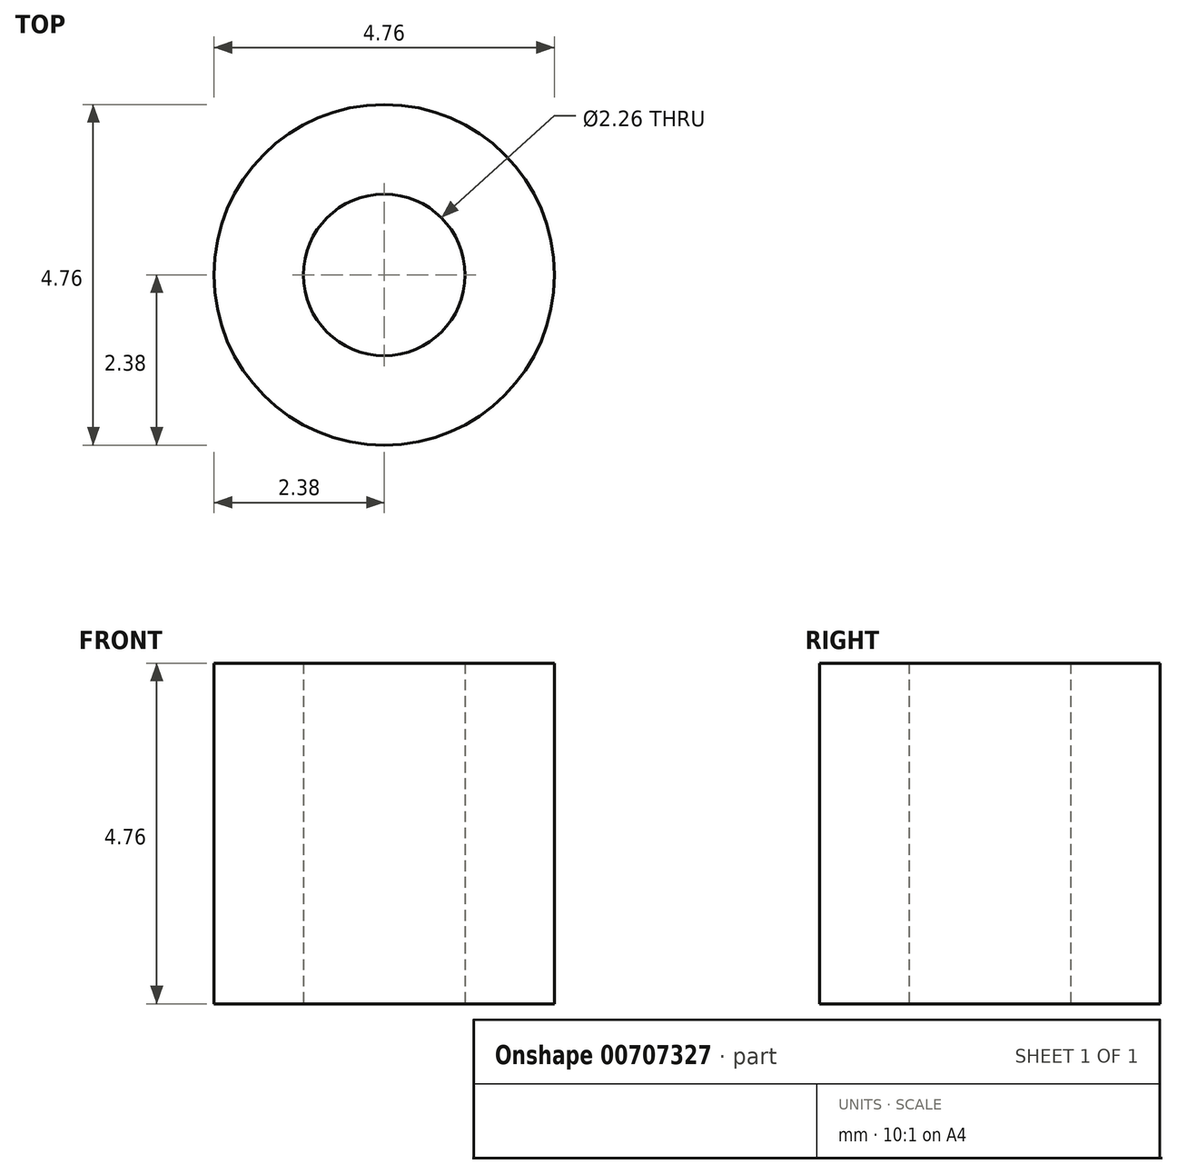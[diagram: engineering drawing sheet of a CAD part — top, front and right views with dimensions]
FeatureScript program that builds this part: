
annotation { "Feature Type Name" : "Feature", "Feature Type Description" : "" }
export const myFeature = defineFeature(function(context is Context, id is Id, definition is map)
    precondition{}
    {
        {
            var Q0;
            Q0=qCreatedBy(makeId("Top.planeOp"),FACE);
            var sketch = newSketch(context, id + "F0", { "sketchPlane" : qUnion([Q0])});
            skCircle(sketch, "E0", {"center": v(0, 0) * mm, "radius": 2.38 * mm});
            skSolve(sketch);
        }
        {
            var Q0;
            Q0=makeQuery(id+"F0.imprint","IMPRINT",FACE,{"disambiguationData":[TD([[makeQuery(id+"F0.imprint","IMPRINT",EDGE,{"derivedFrom":sQuery(id+"F0.wireOp",EDGE,"E0")}),1.0]])]});
            extrude(context, id + "F1", {"entities" : qUnion([Q0]), "depth" : 4.76 * mm, "offsetDistance" : 25.4 * mm});
        }
        {
            var Q0;
            Q0=sQuery(id+"F0.wireOp",VERTEX,"E0.center");
            var Q1;
            Q1=makeQuery(id+"F1.opExtrude","SWEPT_BODY",BODY,{"disambiguationData":[OSD([sQuery(id+"F0.wireOp",EDGE,"E0")])]});
            hole(context, id + "F2", {"style" : HoleStyle.SIMPLE, "endStyle" : HoleEndStyle.THROUGH, "oppositeDirection" : true, "standardTappedOrClearance" : lookupTablePath({ "standard" : "ANSI", "engagement" : "75%", "pitch" : "40 tpi", "size" : "#4", "type" : "Tapped" }), "standardBlindInLast" : lookupTablePath({ "standard" : "ANSI", "engagement" : "75%", "pitch" : "40 tpi", "size" : "#4", "type" : "Tapped" }), "holeDiameter" : 2.26 * mm, "majorDiameter" : 2.84 * mm, "showTappedDepth" : true, "isTappedThrough" : true, "tappedDepth" : 12.7 * mm, "tapClearance" : 3, "startFromSketch" : true, "locations" : qUnion([Q0]), "scope" : qUnion([Q1])});
        }
    });
